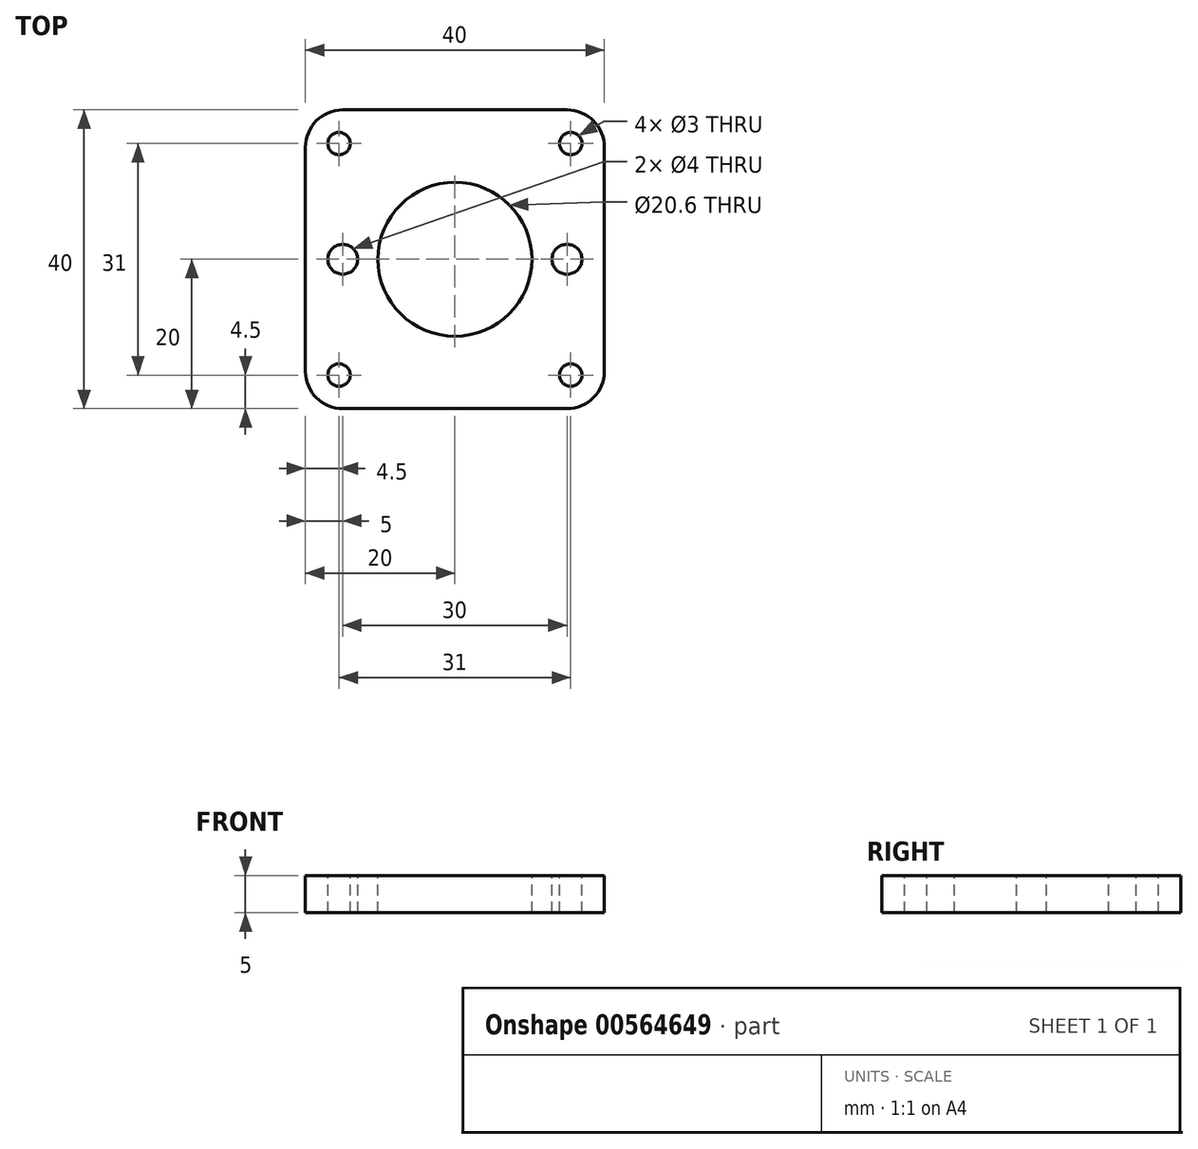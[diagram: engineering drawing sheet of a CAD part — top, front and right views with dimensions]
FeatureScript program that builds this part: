
annotation { "Feature Type Name" : "Feature", "Feature Type Description" : "" }
export const myFeature = defineFeature(function(context is Context, id is Id, definition is map)
    precondition{}
    {
        {
            var Q0;
            Q0=qCreatedBy(makeId("Top.planeOp"),FACE);
            var sketch = newSketch(context, id + "F0", { "sketchPlane" : qUnion([Q0])});
            skLineSegment(sketch, "E0.bottom", {"start": v(20, 20) * mm, "end": v(-20, 20) * mm});
            skLineSegment(sketch, "E0.top", {"start": v(20, -20) * mm, "end": v(-20, -20) * mm});
            skLineSegment(sketch, "E0.left", {"start": v(20, 20) * mm, "end": v(20, -20) * mm});
            skLineSegment(sketch, "E0.right", {"start": v(-20, 20) * mm, "end": v(-20, -20) * mm});
            skPoint(sketch, "E0.middle", {"position": v(0, 0) * mm});
            skSolve(sketch);
        }
        {
            var Q0;
            Q0=makeQuery(id+"F0.imprint","IMPRINT",FACE,{"disambiguationData":[TD([[makeQuery(id+"F0.imprint","IMPRINT",EDGE,{"derivedFrom":sQuery(id+"F0.wireOp",EDGE,"E0.bottom")}),1.0]])]});
            extrude(context, id + "F1", {"entities" : qUnion([Q0]), "depth" : 5 * mm, "offsetDistance" : 25 * mm});
        }
        {
            var Q0;
            Q0=makeQuery(id+"F1.opExtrude","CAP_FACE",FACE,{"disambiguationData":[OSD([sQuery(id+"F0.wireOp",EDGE,"E0.bottom"),sQuery(id+"F0.wireOp",EDGE,"E0.top"),sQuery(id+"F0.wireOp",EDGE,"E0.left"),sQuery(id+"F0.wireOp",EDGE,"E0.right")])],"isStart":false});
            var sketch = newSketch(context, id + "F2", { "sketchPlane" : qUnion([Q0])});
            skCircle(sketch, "E1", {"center": v(0, 0) * mm, "radius": 10.3 * mm});
            skSolve(sketch);
        }
        {
            var Q0;
            Q0=makeQuery(id+"F2.imprint","IMPRINT",FACE,{"disambiguationData":[TD([[makeQuery(id+"F2.imprint","IMPRINT",EDGE,{"derivedFrom":sQuery(id+"F2.wireOp",EDGE,"E1")}),1.0]])]});
            extrude(context, id + "F3", {"entities" : qUnion([Q0]), "operationType" : NewBodyOperationType.REMOVE, "endBound" : BoundingType.THROUGH_ALL, "oppositeDirection" : true, "depth" : 5 * mm, "offsetDistance" : 25 * mm});
        }
        {
            var Q0;
            Q0=makeQuery(id+"F1.opExtrude","CAP_FACE",FACE,{"disambiguationData":[OSD([sQuery(id+"F0.wireOp",EDGE,"E0.bottom"),sQuery(id+"F0.wireOp",EDGE,"E0.top"),sQuery(id+"F0.wireOp",EDGE,"E0.left"),sQuery(id+"F0.wireOp",EDGE,"E0.right")])],"isStart":false});
            var sketch = newSketch(context, id + "F4", { "sketchPlane" : qUnion([Q0])});
            skPoint(sketch, "E2", {"position": v(-15, 0) * mm});
            skPoint(sketch, "E3", {"position": v(15, 0) * mm});
            skSolve(sketch);
        }
        {
            var Q0;
            Q0=makeQuery(id+"F4.imprint","IMPRINT",FACE,{"disambiguationData":[TD([[makeQuery(id+"F4.imprint","IMPRINT",EDGE,{"derivedFrom":makeQuery(id+"F1.opExtrude","CAP_EDGE",EDGE,{"disambiguationData":[OSD([sQuery(id+"F0.wireOp",EDGE,"E0.bottom")])],"isStart":false})}),1.0]])]});
            var sketch = newSketch(context, id + "F5", { "sketchPlane" : qUnion([Q0])});
            skLineSegment(sketch, "E4.bottom", {"start": v(15.5, 15.5) * mm, "end": v(-15.5, 15.5) * mm});
            skLineSegment(sketch, "E4.top", {"start": v(15.5, -15.5) * mm, "end": v(-15.5, -15.5) * mm});
            skLineSegment(sketch, "E4.left", {"start": v(15.5, 15.5) * mm, "end": v(15.5, -15.5) * mm});
            skLineSegment(sketch, "E4.right", {"start": v(-15.5, 15.5) * mm, "end": v(-15.5, -15.5) * mm});
            skPoint(sketch, "E4.middle", {"position": v(0, 0) * mm});
            skPoint(sketch, "E5", {"position": v(-15.5, 15.5) * mm});
            skPoint(sketch, "E6", {"position": v(15.5, 15.5) * mm});
            skPoint(sketch, "E7", {"position": v(15.5, -15.5) * mm});
            skPoint(sketch, "E8", {"position": v(-15.5, -15.5) * mm});
            skSolve(sketch);
        }
        {
            var Q0;
            Q0=sQuery(id+"F5.wireOp",VERTEX,"E5");
            var Q1;
            Q1=sQuery(id+"F5.wireOp",VERTEX,"E6");
            var Q2;
            Q2=sQuery(id+"F5.wireOp",VERTEX,"E7");
            var Q3;
            Q3=sQuery(id+"F5.wireOp",VERTEX,"E8");
            var Q4;
            Q4=makeQuery(id+"F1.opExtrude","SWEPT_BODY",BODY,{"disambiguationData":[OSD([sQuery(id+"F0.wireOp",EDGE,"E0.bottom"),sQuery(id+"F0.wireOp",EDGE,"E0.top"),sQuery(id+"F0.wireOp",EDGE,"E0.left"),sQuery(id+"F0.wireOp",EDGE,"E0.right")])]});
            hole(context, id + "F6", {"style" : HoleStyle.SIMPLE, "endStyle" : HoleEndStyle.THROUGH, "holeDiameter" : 3 * mm, "isTappedThrough" : true, "tappedDepth" : 12 * mm, "tapClearance" : 3, "locations" : qUnion([Q0, Q1, Q2, Q3]), "scope" : qUnion([Q4])});
        }
        {
            var Q0;
            Q0=sQuery(id+"F4.wireOp",VERTEX,"E2");
            var Q1;
            Q1=sQuery(id+"F4.wireOp",VERTEX,"E3");
            var Q2;
            Q2=makeQuery(id+"F1.opExtrude","SWEPT_BODY",BODY,{"disambiguationData":[OSD([sQuery(id+"F0.wireOp",EDGE,"E0.bottom"),sQuery(id+"F0.wireOp",EDGE,"E0.top"),sQuery(id+"F0.wireOp",EDGE,"E0.left"),sQuery(id+"F0.wireOp",EDGE,"E0.right")])]});
            hole(context, id + "F7", {"style" : HoleStyle.SIMPLE, "endStyle" : HoleEndStyle.THROUGH, "holeDiameter" : 4 * mm, "isTappedThrough" : true, "tappedDepth" : 12 * mm, "tapClearance" : 3, "locations" : qUnion([Q0, Q1]), "scope" : qUnion([Q2])});
        }
        {
            var Q0;
            Q0=makeQuery(id+"F1.opExtrude","SWEPT_EDGE",EDGE,{"disambiguationData":[OSD([sQuery(id+"F0.wireOp",EDGE,"E0.bottom"),sQuery(id+"F0.wireOp",EDGE,"E0.right")])]});
            var Q1;
            Q1=makeQuery(id+"F1.opExtrude","SWEPT_EDGE",EDGE,{"disambiguationData":[OSD([sQuery(id+"F0.wireOp",EDGE,"E0.bottom"),sQuery(id+"F0.wireOp",EDGE,"E0.left")])]});
            var Q2;
            Q2=makeQuery(id+"F1.opExtrude","SWEPT_EDGE",EDGE,{"disambiguationData":[OSD([sQuery(id+"F0.wireOp",EDGE,"E0.top"),sQuery(id+"F0.wireOp",EDGE,"E0.right")])]});
            var Q3;
            Q3=makeQuery(id+"F1.opExtrude","SWEPT_EDGE",EDGE,{"disambiguationData":[OSD([sQuery(id+"F0.wireOp",EDGE,"E0.top"),sQuery(id+"F0.wireOp",EDGE,"E0.left")])]});
            fillet(context, id + "F8", {"entities" : qUnion([Q0, Q1, Q2, Q3]), "radius" : 5 * mm, "tangentPropagation" : true, "allowEdgeOverflow" : false});
        }
    });
